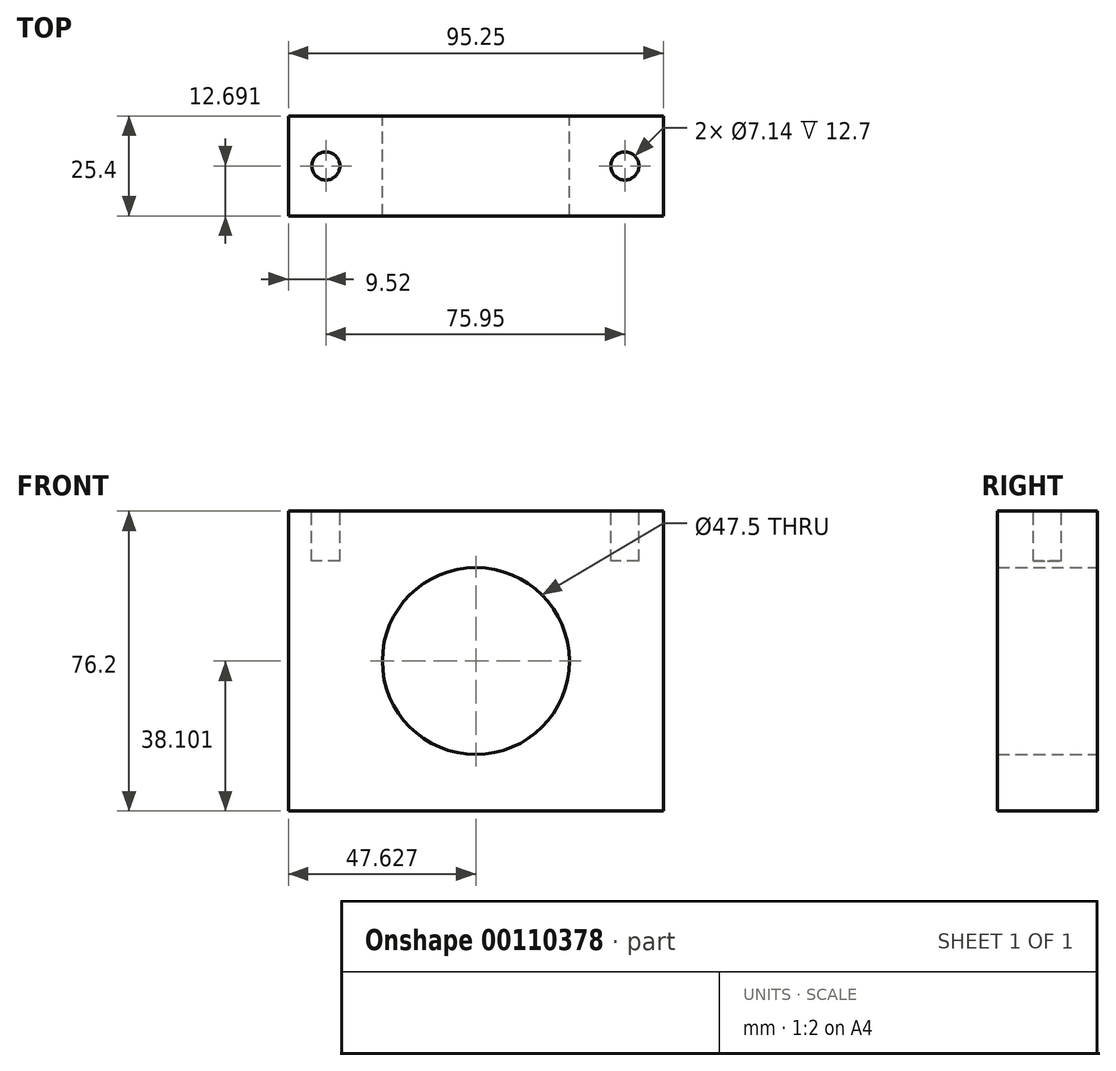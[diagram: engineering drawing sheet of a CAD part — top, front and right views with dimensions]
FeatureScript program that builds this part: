
annotation { "Feature Type Name" : "Feature", "Feature Type Description" : "" }
export const myFeature = defineFeature(function(context is Context, id is Id, definition is map)
    precondition{}
    {
        {
            var Q0;
            Q0=qCreatedBy(makeId("Front.planeOp"),FACE);
            var sketch = newSketch(context, id + "F0", { "sketchPlane" : qUnion([Q0])});
            skLineSegment(sketch, "E0.bottom", {"start": v(-52.66, 50.23) * mm, "end": v(42.6, 50.23) * mm});
            skLineSegment(sketch, "E0.top", {"start": v(-52.66, -25.97) * mm, "end": v(42.6, -25.97) * mm});
            skLineSegment(sketch, "E0.left", {"start": v(-52.66, 50.23) * mm, "end": v(-52.66, -25.97) * mm});
            skLineSegment(sketch, "E0.right", {"start": v(42.6, 50.23) * mm, "end": v(42.6, -25.97) * mm});
            skCircle(sketch, "E1", {"center": v(-5.03, 12.13) * mm, "radius": 23.75 * mm});
            skPoint(sketch, "E1.centerSnap0", {"position": v(-5.03, 50.23) * mm});
            skPoint(sketch, "E1.centerSnap1", {"position": v(-52.66, 12.13) * mm});
            skSolve(sketch);
        }
        {
            var Q0;
            Q0=makeQuery(id+"F0.imprint","IMPRINT",FACE,{"disambiguationData":[TD([[makeQuery(id+"F0.imprint","IMPRINT",EDGE,{"derivedFrom":sQuery(id+"F0.wireOp",EDGE,"E0.bottom")}),-1.0]])]});
            extrude(context, id + "F1", {"entities" : qUnion([Q0]), "depth" : 25.4 * mm});
        }
        {
            var Q0;
            Q0=makeQuery(id+"F1.opExtrude","SWEPT_FACE",FACE,{"disambiguationData":[OSD([sQuery(id+"F0.wireOp",EDGE,"E0.bottom")])]});
            var sketch = newSketch(context, id + "F2", { "sketchPlane" : qUnion([Q0])});
            skSolve(sketch);
        }
        {
            var Q0;
            {var subQ0=sQuery(id+"F0.wireOp",EDGE,"E0.bottom");Q0=makeQuery(id+"F2.imprint","IMPRINT",FACE,{"disambiguationData":[TD([[makeQuery(id+"F2.imprint","IMPRINT",EDGE,{"derivedFrom":makeQuery(id+"F1.opExtrude","CAP_EDGE",EDGE,{"disambiguationData":[OSD([subQ0])],"isStart":true})}),-1.0]])]});}
            var sketch = newSketch(context, id + "F3", { "sketchPlane" : qUnion([Q0])});
            skCircle(sketch, "E2", {"center": v(32.8, -12.7) * mm, "radius": 3.57 * mm});
            skCircle(sketch, "E3", {"center": v(-43.14, -12.7) * mm, "radius": 3.57 * mm});
            skSolve(sketch);
        }
        {
            var Q0;
            Q0 = qSketchRegion(id + "F3", true);
            extrude(context, id + "F4", {"entities" : qUnion([Q0]), "operationType" : NewBodyOperationType.REMOVE, "oppositeDirection" : true, "depth" : 12.7 * mm});
        }
    });
